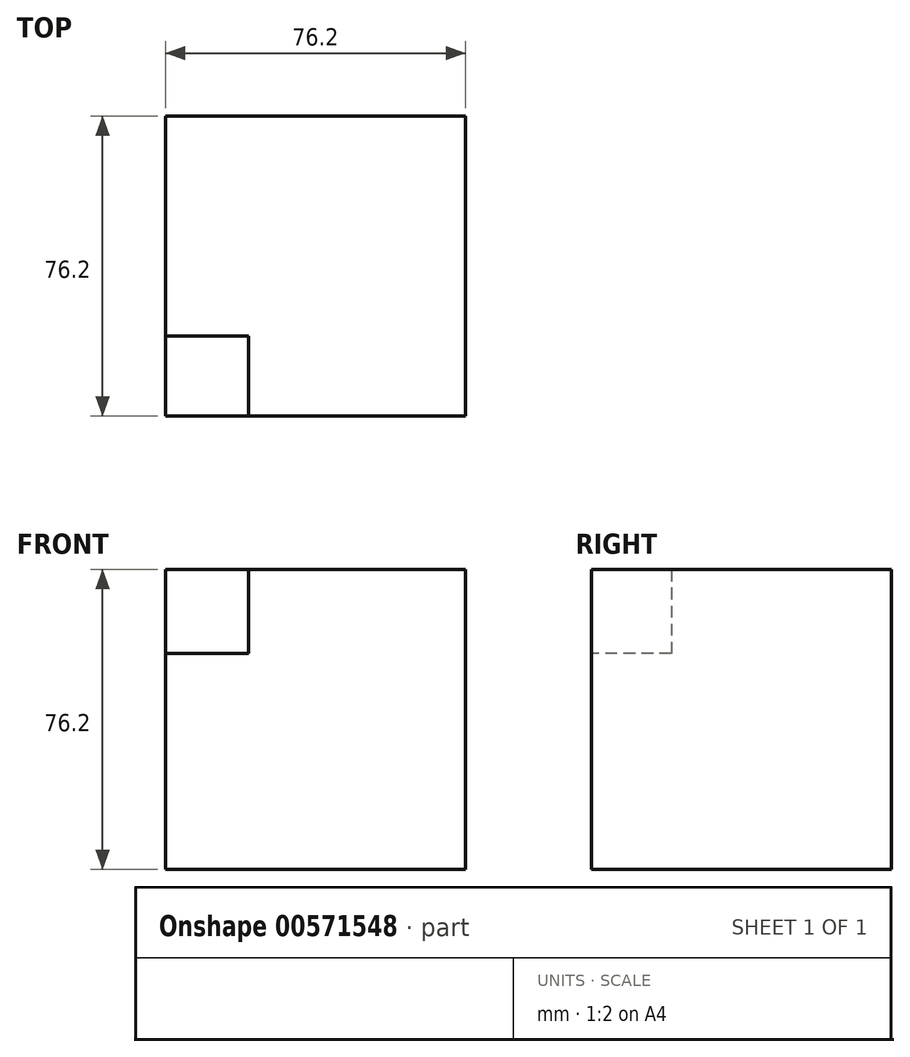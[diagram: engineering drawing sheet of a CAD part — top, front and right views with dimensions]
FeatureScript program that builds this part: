
annotation { "Feature Type Name" : "Feature", "Feature Type Description" : "" }
export const myFeature = defineFeature(function(context is Context, id is Id, definition is map)
    precondition{}
    {
        {
            var Q0;
            Q0=qCreatedBy(makeId("Top.planeOp"),FACE);
            var sketch = newSketch(context, id + "F0", { "sketchPlane" : qUnion([Q0])});
            skLineSegment(sketch, "E0.bottom", {"start": v(-32.03, 38.96) * mm, "end": v(44.17, 38.96) * mm});
            skLineSegment(sketch, "E0.top", {"start": v(-32.03, -37.24) * mm, "end": v(44.17, -37.24) * mm});
            skLineSegment(sketch, "E0.left", {"start": v(-32.03, 38.96) * mm, "end": v(-32.03, -37.24) * mm});
            skLineSegment(sketch, "E0.right", {"start": v(44.17, 38.96) * mm, "end": v(44.17, -37.24) * mm});
            skSolve(sketch);
        }
        {
            var Q0;
            Q0=makeQuery(id+"F0.imprint","IMPRINT",FACE,{"disambiguationData":[TD([[makeQuery(id+"F0.imprint","IMPRINT",EDGE,{"derivedFrom":sQuery(id+"F0.wireOp",EDGE,"E0.bottom")}),-1.0]])]});
            extrude(context, id + "F1", {"entities" : qUnion([Q0]), "depth" : 76.2 * mm, "offsetDistance" : 25.4 * mm});
        }
        {
            var Q0;
            Q0=makeQuery(id+"F1.opExtrude","SWEPT_FACE",FACE,{"disambiguationData":[OSD([sQuery(id+"F0.wireOp",EDGE,"E0.top")])]});
            var sketch = newSketch(context, id + "F2", { "sketchPlane" : qUnion([Q0])});
            skLineSegment(sketch, "E1.bottom", {"start": v(-32.03, 76.2) * mm, "end": v(-10.95, 76.2) * mm});
            skLineSegment(sketch, "E1.top", {"start": v(-32.03, 54.86) * mm, "end": v(-10.95, 54.86) * mm});
            skLineSegment(sketch, "E1.left", {"start": v(-32.03, 76.2) * mm, "end": v(-32.03, 54.86) * mm});
            skLineSegment(sketch, "E1.right", {"start": v(-10.95, 76.2) * mm, "end": v(-10.95, 54.86) * mm});
            skSolve(sketch);
        }
        {
            var Q0;
            Q0=makeQuery(id+"F2.imprint","IMPRINT",FACE,{"disambiguationData":[TD([[makeQuery(id+"F2.imprint","IMPRINT",EDGE,{"derivedFrom":sQuery(id+"F2.wireOp",EDGE,"E1.bottom")}),-1.0]])]});
            extrude(context, id + "F3", {"entities" : qUnion([Q0]), "operationType" : NewBodyOperationType.REMOVE, "oppositeDirection" : true, "depth" : 20.32 * mm, "offsetDistance" : 25.4 * mm});
        }
    });
